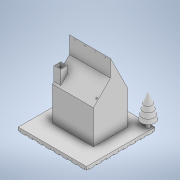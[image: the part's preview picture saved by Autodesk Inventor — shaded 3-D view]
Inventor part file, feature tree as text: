
AUTODESK INVENTOR PART (.ipt)
format: ipt  version: 2022.4 (Build 264492010, 492A)  size: 6,498,816 bytes
history: native  units: mm
features: other x244, sketch x1
ambient origin geometry x8: Origin, YZ Plane, XZ Plane, XY Plane, X Axis, Y Axis, Z Axis, Center Point
bodies: Solid1 (feature_tree)
feature tree (245):
  other  "House_Assembly_Depth_Tracking.iam"
  other  "Tile.ipt:1"
  other  "Tile_Connector.ipt:1"
  other  "Tile_Connector.ipt:2"
  other  "Tile_Connector.ipt:3"
  other  "Tile.ipt:2"
  other  "Tile_Connector.ipt:4"
  other  "Tile_Connector.ipt:5"
  other  "Tile.ipt:3"
  other  "Tile_Connector.ipt:6"
  other  "Tile_Connector.ipt:7"
  other  "Tile.ipt:4"
  other  "Tile_Connector.ipt:9"
  other  "Tile.ipt:5"
  other  "Tile_Connector.ipt:10"
  other  "Tile_Connector.ipt:11"
  other  "Tile.ipt:6"
  other  "Tile_Connector.ipt:12"
  other  "Tile_Connector.ipt:13"
  other  "Tile.ipt:7"
  other  "Tile_Connector.ipt:14"
  other  "Tile_Connector.ipt:15"
  other  "Tile.ipt:8"
  other  "Tile_Connector.ipt:17"
  other  "Tile.ipt:9"
  other  "Tile_Connector.ipt:18"
  other  "Tile_Connector.ipt:19"
  other  "Tile.ipt:10"
  other  "Tile_Connector.ipt:20"
  other  "Tile_Connector.ipt:21"
  other  "Tile.ipt:11"
  other  "Tile_Connector.ipt:22"
  other  "Tile_Connector.ipt:23"
  other  "Tile.ipt:12"
  other  "Tile.ipt:13"
  other  "Tile_Connector.ipt:26"
  other  "Tile.ipt:14"
  other  "Tile_Connector.ipt:28"
  other  "Tile.ipt:15"
  other  "Tile_Connector.ipt:30"
  other  "Tile.ipt:16"
  other  "Wall.ipt:1"
  other  "Wall.ipt:2"
  other  "Wall.ipt:3"
  other  "Wall.ipt:4"
  other  "Roof_Wall_Small_Left.ipt:2"
  other  "Roof_Wall_Small_Right.ipt:2"
  other  "Roof_Wall_Large_Left.ipt:1"
  other  "Roof_Wall_Large_Right.ipt:1"
  other  "Roof_Small.ipt:1"
  other  "Roof_Large.ipt:1"
  other  "Hanging_Wall.ipt:1"
  other  "Tile_Cover.ipt:1"
  other  "Tree_Leaves.ipt:1"
  other  "Tree_Trunk.ipt:1"
  other  "Chimney.ipt:1"
  other  "Pin.ipt:1"
  other  "Tile_Cover.ipt:2"
  other  "Tile_Cover.ipt:3"
  other  "Tile_Cover.ipt:4"
  other  "1x1_Piece.ipt:145"
  other  "1x1_Piece.ipt:146"
  other  "1x1_Piece.ipt:147"
  other  "1x1_Piece.ipt:148"
  other  "1x1_Piece.ipt:151"
  other  "1x1_Piece.ipt:155"
  other  "1x1_Piece.ipt:156"
  other  "1x1_Piece.ipt:157"
  other  "1x1_Piece.ipt:158"
  other  "1x1_Piece.ipt:159"
  other  "1x1_Piece.ipt:160"
  other  "1x1_Piece.ipt:161"
  other  "1x1_Piece.ipt:162"
  other  "1x1_Piece.ipt:163"
  other  "1x1_Piece.ipt:164"
  other  "1x1_Piece.ipt:165"
  other  "1x1_Piece.ipt:166"
  other  "1x1_Piece.ipt:167"
  other  "1x1_Piece.ipt:168"
  other  "1x1_Piece.ipt:169"
  other  "1x1_Piece.ipt:170"
  other  "1x1_Piece.ipt:171"
  other  "1x1_Piece.ipt:172"
  other  "1x1_Piece.ipt:173"
  other  "1x1_Piece.ipt:174"
  other  "1x1_Piece.ipt:175"
  other  "1x1_Piece.ipt:176"
  other  "1x1_Piece.ipt:177"
  other  "1x1_Piece.ipt:178"
  other  "1x1_Piece.ipt:179"
  other  "1x1_Piece.ipt:180"
  other  "1x1_Piece.ipt:181"
  other  "1x1_Piece.ipt:182"
  other  "1x1_Piece.ipt:183"
  other  "1x1_Piece.ipt:184"
  other  "1x1_Piece.ipt:185"
  other  "1x1_Piece.ipt:186"
  other  "1x1_Piece.ipt:187"
  other  "1x1_Piece.ipt:188"
  other  "1x1_Piece.ipt:189"
  other  "1x1_Piece.ipt:190"
  other  "1x1_Piece.ipt:191"
  other  "1x1_Piece.ipt:192"
  other  "1x1_Piece.ipt:193"
  other  "1x1_Piece.ipt:194"
  other  "1x1_Piece.ipt:195"
  other  "1x1_Piece.ipt:196"
  other  "1x1_Piece.ipt:197"
  other  "1x1_Piece.ipt:198"
  other  "1x1_Piece.ipt:199"
  other  "1x1_Piece.ipt:200"
  other  "1x1_Piece.ipt:201"
  other  "1x1_Piece.ipt:202"
  other  "1x1_Piece.ipt:203"
  other  "1x1_Piece.ipt:204"
  other  "1x1_Piece.ipt:205"
  other  "1x1_Piece.ipt:206"
  other  "1x1_Piece.ipt:207"
  other  "1x1_Piece.ipt:208"
  other  "1x1_Piece.ipt:209"
  other  "1x1_Piece.ipt:210"
  other  "1x1_Piece.ipt:211"
  other  "1x1_Piece.ipt:212"
  other  "1x1_Piece.ipt:213"
  other  "1x1_Piece.ipt:214"
  other  "1x1_Piece.ipt:215"
  other  "1x1_Piece.ipt:216"
  other  "1x1_Piece.ipt:217"
  other  "1x1_Piece.ipt:218"
  other  "1x1_Piece.ipt:219"
  other  "1x1_Piece.ipt:220"
  other  "1x1_Piece.ipt:221"
  other  "1x1_Piece.ipt:222"
  other  "1x1_Piece.ipt:223"
  other  "1x1_Piece.ipt:224"
  other  "1x1_Piece.ipt:225"
  other  "1x1_Piece.ipt:226"
  other  "1x1_Piece.ipt:227"
  other  "1x1_Piece.ipt:228"
  other  "1x1_Piece.ipt:229"
  other  "1x1_Piece.ipt:230"
  other  "1x1_Piece.ipt:231"
  other  "1x1_Piece.ipt:232"
  other  "1x1_Piece.ipt:233"
  other  "1x1_Piece.ipt:234"
  other  "1x1_Piece.ipt:235"
  other  "1x1_Piece.ipt:236"
  other  "1x1_Piece.ipt:237"
  other  "1x1_Piece.ipt:238"
  other  "1x1_Piece.ipt:239"
  other  "1x1_Piece.ipt:240"
  other  "1x1_Piece.ipt:241"
  other  "1x1_Piece.ipt:242"
  other  "1x1_Piece.ipt:243"
  other  "1x1_Piece.ipt:244"
  other  "1x1_Piece.ipt:245"
  other  "1x1_Piece.ipt:246"
  other  "1x1_Piece.ipt:247"
  other  "1x1_Piece.ipt:248"
  other  "1x1_Piece.ipt:249"
  other  "1x1_Piece.ipt:250"
  other  "1x1_Piece.ipt:251"
  other  "1x1_Piece.ipt:252"
  other  "1x1_Piece.ipt:253"
  other  "1x1_Piece.ipt:254"
  other  "1x1_Piece.ipt:255"
  other  "1x1_Piece.ipt:256"
  other  "1x1_Piece.ipt:257"
  other  "1x1_Piece.ipt:258"
  other  "1x1_Piece.ipt:259"
  other  "1x1_Piece.ipt:260"
  other  "1x1_Piece.ipt:261"
  other  "1x1_Piece.ipt:262"
  other  "1x1_Piece.ipt:263"
  other  "1x1_Piece.ipt:264"
  other  "1x1_Piece.ipt:265"
  other  "1x1_Piece.ipt:266"
  other  "1x1_Piece.ipt:267"
  other  "1x1_Piece.ipt:268"
  other  "1x1_Piece.ipt:269"
  other  "1x1_Piece.ipt:270"
  other  "1x1_Piece.ipt:271"
  other  "1x1_Piece.ipt:272"
  other  "1x1_Piece.ipt:273"
  other  "1x1_Piece.ipt:274"
  other  "1x1_Piece.ipt:275"
  other  "1x1_Piece.ipt:276"
  other  "1x1_Piece.ipt:277"
  other  "1x1_Piece.ipt:278"
  other  "1x1_Piece.ipt:279"
  other  "1x1_Piece.ipt:280"
  other  "1x1_Piece.ipt:281"
  other  "1x1_Piece.ipt:282"
  other  "1x1_Piece.ipt:283"
  other  "1x1_Piece.ipt:284"
  other  "1x1_Piece.ipt:285"
  other  "1x1_Piece.ipt:286"
  other  "1x1_Piece.ipt:287"
  other  "1x1_Piece.ipt:288"
  other  "1x1_Piece.ipt:289"
  other  "1x1_Piece.ipt:290"
  other  "1x1_Piece.ipt:291"
  other  "1x1_Piece.ipt:292"
  other  "1x1_Piece.ipt:293"
  other  "1x1_Piece.ipt:294"
  other  "1x1_Piece.ipt:295"
  other  "1x1_Piece.ipt:296"
  other  "1x1_Piece.ipt:297"
  other  "1x1_Piece.ipt:298"
  other  "1x1_Piece.ipt:299"
  other  "1x1_Piece.ipt:300"
  other  "1x1_Piece.ipt:301"
  other  "1x1_Piece.ipt:302"
  other  "1x1_Piece.ipt:303"
  other  "1x1_Piece.ipt:304"
  other  "1x1_Piece.ipt:305"
  other  "1x1_Piece.ipt:306"
  other  "1x1_Piece.ipt:307"
  other  "1x1_Piece.ipt:308"
  other  "1x1_Piece.ipt:309"
  other  "1x1_Piece.ipt:310"
  other  "1x1_Piece.ipt:311"
  other  "1x1_Piece.ipt:312"
  other  "1x1_Piece.ipt:313"
  other  "1x1_Piece.ipt:314"
  other  "1x1_Piece.ipt:315"
  other  "1x1_Piece.ipt:316"
  other  "1x1_Piece.ipt:317"
  other  "1x1_Piece.ipt:318"
  other  "1x1_Piece.ipt:319"
  other  "1x1_Piece.ipt:320"
  other  "1x1_Piece.ipt:321"
  other  "1x1_Piece.ipt:322"
  other  "1x1_Piece.ipt:323"
  other  "1x1_Piece.ipt:324"
  other  "1x1_Piece.ipt:325"
  other  "Rail_Clip_Left.ipt:1"
  other  "Rail_Clip_Right.ipt:1"
  other  "Roof_Pin_Clip.ipt:1"
  other  "Roof_Pin_Clip.ipt:2"
  other  "Roof_Pin_Clip.ipt:3"
  other  "Roof_Pin_Clip.ipt:4"
  other  "Roof_Pin_Clip.ipt:5"
  other  "Roof_Pin_Clip.ipt:6"
  sketch  "Sketch5"  dims[d0=10.0mm]
